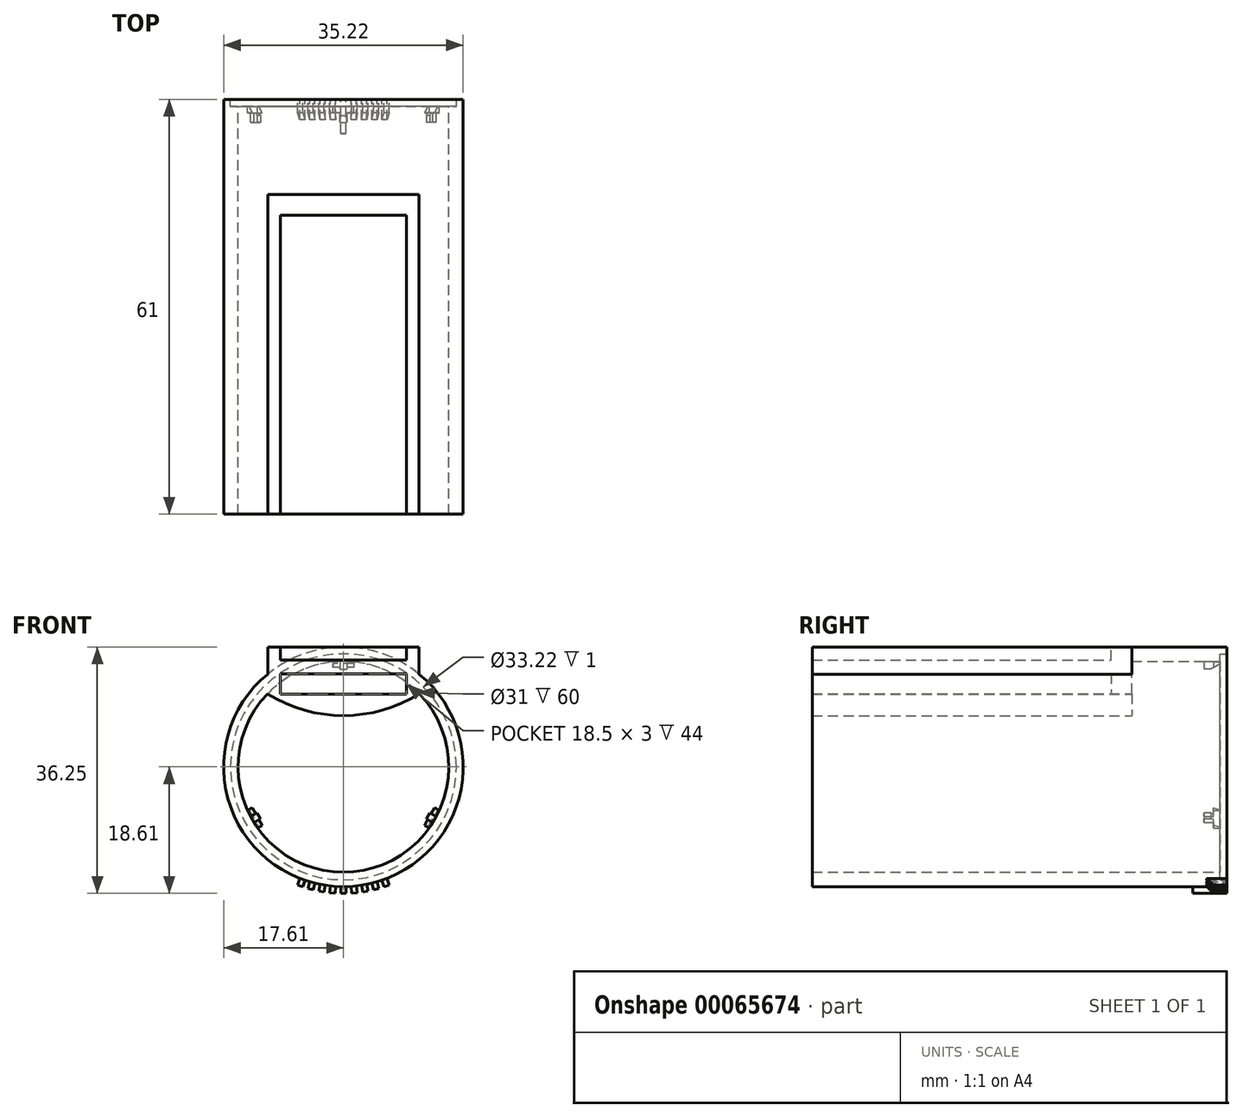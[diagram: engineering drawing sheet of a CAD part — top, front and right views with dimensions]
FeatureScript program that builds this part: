
annotation { "Feature Type Name" : "Feature", "Feature Type Description" : "" }
export const myFeature = defineFeature(function(context is Context, id is Id, definition is map)
    precondition{}
    {
        {
            var Q0;
            Q0=qCreatedBy(makeId("Front.planeOp"),FACE);
            var sketch = newSketch(context, id + "F0", { "sketchPlane" : qUnion([Q0])});
            skCircle(sketch, "E0", {"center": v(0, 0) * mm, "radius": 15.5 * mm});
            skCircle(sketch, "E1", {"center": v(0, 0) * mm, "radius": 17.6 * mm});
            skCircle(sketch, "E2", {"center": v(0, 0) * mm, "radius": 16.6 * mm});
            skPoint(sketch, "E3", {"position": v(0, 14.4) * mm});
            skLineSegment(sketch, "E4", {"start": v(0, 0) * mm, "end": v(0, 14.4) * mm, "construction": true});
            skSolve(sketch);
        }
        {
            var Q0;
            Q0=makeQuery(id+"F0.imprint","IMPRINT",FACE,{"disambiguationData":[TD([[makeQuery(id+"F0.imprint","IMPRINT",EDGE,{"derivedFrom":sQuery(id+"F0.wireOp",EDGE,"E1")}),1.0]])]});
            var sketch = newSketch(context, id + "F1", { "sketchPlane" : qUnion([Q0])});
            skCircle(sketch, "E5.0", {"center": v(0, 0) * mm, "radius": 17.6 * mm, "construction": true});
            skLineSegment(sketch, "E6", {"start": v(0, 0) * mm, "end": v(12.73, -34.98) * mm, "construction": true});
            skPoint(sketch, "E7", {"position": v(6.36, -17.49) * mm});
            skLineSegment(sketch, "E8", {"start": v(6.74, -17.35) * mm, "end": v(5.99, -17.62) * mm});
            skLineSegment(sketch, "E9", {"start": v(6.74, -17.35) * mm, "end": v(6.4, -16.4) * mm});
            skLineSegment(sketch, "E10", {"start": v(5.99, -17.62) * mm, "end": v(5.65, -16.68) * mm});
            skPoint(sketch, "E11.1.0", {"position": v(4.82, -17.98) * mm});
            skLineSegment(sketch, "E11.1.1", {"start": v(5.2, -17.87) * mm, "end": v(4.94, -16.9) * mm});
            skLineSegment(sketch, "E11.1.2", {"start": v(4.43, -18.08) * mm, "end": v(4.17, -17.1) * mm});
            skLineSegment(sketch, "E11.1.3", {"start": v(5.2, -17.87) * mm, "end": v(4.43, -18.08) * mm});
            skPoint(sketch, "E11.2.0", {"position": v(3.23, -18.33) * mm});
            skLineSegment(sketch, "E11.2.1", {"start": v(3.63, -18.26) * mm, "end": v(3.45, -17.27) * mm});
            skLineSegment(sketch, "E11.2.2", {"start": v(2.84, -18.4) * mm, "end": v(2.66, -17.4) * mm});
            skLineSegment(sketch, "E11.2.3", {"start": v(3.63, -18.26) * mm, "end": v(2.84, -18.4) * mm});
            skPoint(sketch, "E11.3.0", {"position": v(1.62, -18.54) * mm});
            skLineSegment(sketch, "E11.3.1", {"start": v(2.02, -18.5) * mm, "end": v(1.93, -17.5) * mm});
            skLineSegment(sketch, "E11.3.2", {"start": v(1.22, -18.57) * mm, "end": v(1.14, -17.57) * mm});
            skLineSegment(sketch, "E11.3.3", {"start": v(2.02, -18.5) * mm, "end": v(1.22, -18.57) * mm});
            skPoint(sketch, "E11.4.0", {"position": v(0, -18.61) * mm});
            skLineSegment(sketch, "E11.4.1", {"start": v(0.4, -18.61) * mm, "end": v(0.4, -17.6) * mm});
            skLineSegment(sketch, "E11.4.2", {"start": v(-0.4, -18.61) * mm, "end": v(-0.4, -17.6) * mm});
            skLineSegment(sketch, "E11.4.3", {"start": v(0.4, -18.61) * mm, "end": v(-0.4, -18.61) * mm});
            skPoint(sketch, "E11.5.0", {"position": v(-1.62, -18.54) * mm});
            skLineSegment(sketch, "E11.5.1", {"start": v(-1.22, -18.57) * mm, "end": v(-1.14, -17.57) * mm});
            skLineSegment(sketch, "E11.5.2", {"start": v(-2.02, -18.5) * mm, "end": v(-1.93, -17.5) * mm});
            skLineSegment(sketch, "E11.5.3", {"start": v(-1.22, -18.57) * mm, "end": v(-2.02, -18.5) * mm});
            skPoint(sketch, "E11.6.0", {"position": v(-3.23, -18.33) * mm});
            skLineSegment(sketch, "E11.6.1", {"start": v(-2.84, -18.4) * mm, "end": v(-2.66, -17.4) * mm});
            skLineSegment(sketch, "E11.6.2", {"start": v(-3.63, -18.26) * mm, "end": v(-3.45, -17.27) * mm});
            skLineSegment(sketch, "E11.6.3", {"start": v(-2.84, -18.4) * mm, "end": v(-3.63, -18.26) * mm});
            skPoint(sketch, "E11.7.0", {"position": v(-4.82, -17.98) * mm});
            skLineSegment(sketch, "E11.7.1", {"start": v(-4.43, -18.08) * mm, "end": v(-4.17, -17.1) * mm});
            skLineSegment(sketch, "E11.7.2", {"start": v(-5.2, -17.87) * mm, "end": v(-4.94, -16.9) * mm});
            skLineSegment(sketch, "E11.7.3", {"start": v(-4.43, -18.08) * mm, "end": v(-5.2, -17.87) * mm});
            skPoint(sketch, "E11.8.0", {"position": v(-6.36, -17.49) * mm});
            skLineSegment(sketch, "E11.8.1", {"start": v(-5.99, -17.62) * mm, "end": v(-5.65, -16.68) * mm});
            skLineSegment(sketch, "E11.8.2", {"start": v(-6.74, -17.35) * mm, "end": v(-6.4, -16.4) * mm});
            skLineSegment(sketch, "E11.8.3", {"start": v(-5.99, -17.62) * mm, "end": v(-6.74, -17.35) * mm});
            skLineSegment(sketch, "E11.anchor1", {"start": v(0, 0) * mm, "end": v(6.36, -17.49) * mm, "construction": true});
            skLineSegment(sketch, "E11.anchor2", {"start": v(0, 0) * mm, "end": v(-6.36, -17.49) * mm, "construction": true});
            skSolve(sketch);
        }
        {
            var Q0;
            Q0=qCreatedBy(makeId("Front.planeOp"),FACE);
            cPlane(context, id + "F2", {"entities" : qUnion([Q0]), "cplaneType" : CPlaneType.OFFSET, "offset" : 17 * mm, "width" : 150 * mm, "height" : 150 * mm});
        }
        {
            var Q0;
            Q0=qCreatedBy(id+"F2.planeOp",FACE);
            var sketch = newSketch(context, id + "F3", { "sketchPlane" : qUnion([Q0])});
            skLineSegment(sketch, "E12.rect.bottom", {"start": v(-9.25, 13.7) * mm, "end": v(9.25, 13.7) * mm});
            skLineSegment(sketch, "E12.rect.top", {"start": v(-9.25, 10.7) * mm, "end": v(9.25, 10.7) * mm});
            skLineSegment(sketch, "E12.rect.left", {"start": v(-9.25, 13.7) * mm, "end": v(-9.25, 10.7) * mm});
            skLineSegment(sketch, "E12.rect.right", {"start": v(9.25, 13.7) * mm, "end": v(9.25, 10.7) * mm});
            skPoint(sketch, "E12.rect.middle", {"position": v(0, 12.2) * mm});
            skLineSegment(sketch, "E13.rect.bottom", {"start": v(-6.75, 13.7) * mm, "end": v(6.75, 13.7) * mm});
            skLineSegment(sketch, "E13.rect.top", {"start": v(-6.75, 15.7) * mm, "end": v(6.75, 15.7) * mm});
            skLineSegment(sketch, "E13.rect.left", {"start": v(-6.75, 13.7) * mm, "end": v(-6.75, 15.7) * mm});
            skLineSegment(sketch, "E13.rect.right", {"start": v(6.75, 13.7) * mm, "end": v(6.75, 15.7) * mm});
            skPoint(sketch, "E13.rect.middle", {"position": v(0, 14.7) * mm});
            skLineSegment(sketch, "E14.rect.bottom", {"start": v(9.25, 15.7) * mm, "end": v(-9.25, 15.7) * mm});
            skLineSegment(sketch, "E14.rect.top", {"start": v(9.25, 18.83) * mm, "end": v(-9.25, 18.83) * mm});
            skLineSegment(sketch, "E14.rect.left", {"start": v(9.25, 15.7) * mm, "end": v(9.25, 18.83) * mm});
            skLineSegment(sketch, "E14.rect.right", {"start": v(-9.25, 15.7) * mm, "end": v(-9.25, 18.83) * mm});
            skPoint(sketch, "E14.rect.middle", {"position": v(0, 17.26) * mm});
            skPoint(sketch, "E14.rect.middle.positionSnap0", {"position": v(0, 15.7) * mm});
            skPoint(sketch, "E14.rect.cornerSnap0", {"position": v(0, 15.7) * mm});
            skPoint(sketch, "E14.rect.centerSnap0", {"position": v(0, 15.7) * mm});
            skSolve(sketch);
        }
        {
            var Q0;
            Q0=qCreatedBy(id+"F2.planeOp",FACE);
            var sketch = newSketch(context, id + "F4", { "sketchPlane" : qUnion([Q0])});
            skLineSegment(sketch, "E15.rect.bottom", {"start": v(-11.14, 17.64) * mm, "end": v(11.14, 17.64) * mm});
            skLineSegment(sketch, "E15.rect.top", {"start": v(-11.14, 10.71) * mm, "end": v(11.14, 10.71) * mm});
            skLineSegment(sketch, "E15.rect.left", {"start": v(-11.14, 17.64) * mm, "end": v(-11.14, 10.71) * mm});
            skLineSegment(sketch, "E15.rect.right", {"start": v(11.14, 17.64) * mm, "end": v(11.14, 10.71) * mm});
            skPoint(sketch, "E15.rect.middle", {"position": v(0, 14.18) * mm});
            skArc(sketch, "E16", {"start": v(-11.14, 10.71) * mm, "mid": v(0, 7.54) * mm, "end": v(11.14, 10.71) * mm});
            skPoint(sketch, "E16.third.point", {"position": v(-1.83, 7.62) * mm});
            skSolve(sketch);
        }
        {
            var Q0;
            Q0=makeQuery(id+"F0.imprint","IMPRINT",FACE,{"disambiguationData":[TD([[makeQuery(id+"F0.imprint","IMPRINT",EDGE,{"derivedFrom":sQuery(id+"F0.wireOp",EDGE,"E1")}),1.0]])]});
            extrude(context, id + "F5", {"entities" : qUnion([Q0]), "depth" : 61 * mm});
        }
        {
            var Q0;
            Q0=makeQuery(id+"F0.imprint","IMPRINT",FACE,{"disambiguationData":[TD([[makeQuery(id+"F0.imprint","IMPRINT",EDGE,{"derivedFrom":sQuery(id+"F0.wireOp",EDGE,"E0")}),-1.0]])]});
            var Q1;
            Q1=makeQuery(id+"F5.opExtrude","CAP_FACE",FACE,{"disambiguationData":[OSD([sQuery(id+"F0.wireOp",EDGE,"E1"),sQuery(id+"F0.wireOp",EDGE,"E2")])],"isStart":false});
            extrude(context, id + "F6", {"entities" : qUnion([Q0]), "operationType" : NewBodyOperationType.ADD, "endBound" : BoundingType.UP_TO_SURFACE, "endBoundEntityFace" : qUnion([Q1]), "depth" : 25 * mm, "hasSecondDirection" : true, "secondDirectionOppositeDirection" : false, "secondDirectionDepth" : 1 * mm});
        }
        {
            var Q0;
            Q0=sQuery(id+"F0.wireOp",VERTEX,"E3");
            var Q1;
            Q1=sQuery(id+"F0.wireOp",EDGE,"E4");
            cPlane(context, id + "F7", {"entities" : qUnion([Q0, Q1]), "cplaneType" : CPlaneType.LINE_POINT, "offset" : 150 * mm, "width" : 150 * mm, "height" : 150 * mm});
        }
        {
            var Q0;
            Q0=qCreatedBy(id+"F7.planeOp",FACE);
            var sketch = newSketch(context, id + "F8", { "sketchPlane" : qUnion([Q0])});
            skPoint(sketch, "E17.orphan", {"position": v(-15.5, -1) * mm});
            skPoint(sketch, "E18.orphan", {"position": v(15.5, -1) * mm});
            skLineSegment(sketch, "E19", {"start": v(-0.5, -3.4) * mm, "end": v(0, -3.4) * mm});
            skLineSegment(sketch, "E20", {"start": v(-0.5, -2) * mm, "end": v(-0.5, -3.4) * mm});
            skLineSegment(sketch, "E21", {"start": v(-0.5, -2) * mm, "end": v(-1.5, -2) * mm});
            skLineSegment(sketch, "E22", {"start": v(-1.5, -1) * mm, "end": v(-1.5, -2) * mm});
            skLineSegment(sketch, "E23", {"start": v(-1.5, -1) * mm, "end": v(0, -1) * mm});
            skLineSegment(sketch, "E24", {"start": v(0, -3.4) * mm, "end": v(0, 0) * mm, "construction": true});
            skLineSegment(sketch, "E25.MirrorCS", {"start": v(1.5, -1) * mm, "end": v(0, -1) * mm});
            skLineSegment(sketch, "E26.MirrorCS", {"start": v(1.5, -1) * mm, "end": v(1.5, -2) * mm});
            skLineSegment(sketch, "E27.MirrorCS", {"start": v(0.5, -2) * mm, "end": v(1.5, -2) * mm});
            skLineSegment(sketch, "E28.MirrorCS", {"start": v(0.5, -2) * mm, "end": v(0.5, -3.4) * mm});
            skLineSegment(sketch, "E29.MirrorCS", {"start": v(0.5, -3.4) * mm, "end": v(0, -3.4) * mm});
            skLineSegment(sketch, "E30.0", {"start": v(15.5, -1) * mm, "end": v(-15.5, -1) * mm, "construction": true});
            skSolve(sketch);
        }
        {
            var Q0;
            Q0=makeQuery(id+"F8.imprint","IMPRINT",FACE,{"disambiguationData":[TD([[makeQuery(id+"F8.imprint","IMPRINT",EDGE,{"derivedFrom":sQuery(id+"F8.wireOp",EDGE,"E19")}),1.0]])]});
            var Q1;
            Q1=makeQuery(id+"F6.opExtrude","SWEPT_FACE",FACE,{"disambiguationData":[OSD([sQuery(id+"F0.wireOp",EDGE,"E0")])]});
            extrude(context, id + "F9", {"entities" : qUnion([Q0]), "endBound" : BoundingType.UP_TO_SURFACE, "endBoundEntityFace" : qUnion([Q1]), "depth" : 25 * mm});
        }
        {
            var Q0;
            Q0=makeQuery(id+"F9.opExtrude","CAP_EDGE",EDGE,{"disambiguationData":[OSD([sQuery(id+"F8.wireOp",EDGE,"E23"),sQuery(id+"F8.wireOp",EDGE,"E25.MirrorCS")])],"isStart":true});
            chamfer(context, id + "F10", {"entities" : qUnion([Q0]), "chamferType" : ChamferType.OFFSET_ANGLE, "width" : 0.8 * mm, "oppositeDirection" : false, "angle" : 60 * degree, "tangentPropagation" : true});
        }
        {
            var Q0;
            Q0=qCreatedBy(makeId("Right.planeOp"),FACE);
            var sketch = newSketch(context, id + "F11", { "sketchPlane" : qUnion([Q0])});
            skLineSegment(sketch, "E31", {"start": v(0, 0) * mm, "end": v(-69.37, 0) * mm, "construction": true});
            skSolve(sketch);
        }
        {
            var Q0;
            Q0=makeQuery(id+"F9.opExtrude","SWEPT_BODY",BODY,{"disambiguationData":[OSD([sQuery(id+"F8.wireOp",EDGE,"E19"),sQuery(id+"F8.wireOp",EDGE,"E20"),sQuery(id+"F8.wireOp",EDGE,"E21"),sQuery(id+"F8.wireOp",EDGE,"E22"),sQuery(id+"F8.wireOp",EDGE,"E23"),sQuery(id+"F8.wireOp",EDGE,"E25.MirrorCS"),sQuery(id+"F8.wireOp",EDGE,"E26.MirrorCS"),sQuery(id+"F8.wireOp",EDGE,"E27.MirrorCS"),sQuery(id+"F8.wireOp",EDGE,"E28.MirrorCS"),sQuery(id+"F8.wireOp",EDGE,"E29.MirrorCS")])]});
            var Q1;
            Q1=sQuery(id+"F11.wireOp",EDGE,"E31");
            circularPattern(context, id + "F12", {"entities" : qUnion([Q0]), "axis" : qUnion([Q1]), "angle" : 360 * degree, "instanceCount" : 3, "equalSpace" : true});
        }
        {
            var Q0;
            Q0=makeQuery(id+"F4.imprint","IMPRINT",FACE,{"disambiguationData":[TD([[makeQuery(id+"F4.imprint","IMPRINT",EDGE,{"derivedFrom":sQuery(id+"F4.wireOp",EDGE,"E15.rect.bottom")}),-1.0]])]});
            var Q1;
            Q1=makeQuery(id+"F4.imprint","IMPRINT",FACE,{"disambiguationData":[TD([[makeQuery(id+"F4.imprint","IMPRINT",EDGE,{"derivedFrom":sQuery(id+"F4.wireOp",EDGE,"E15.rect.top")}),-1.0]])]});
            var Q2;
            {var subQ0=sQuery(id+"F0.wireOp",EDGE,"E2");Q2=makeQuery(id+"F6.boolean.opBoolean","MERGE",FACE,{"derivedFrom":[makeQuery(id+"F5.opExtrude","CAP_FACE",FACE,{"disambiguationData":[OSD([sQuery(id+"F0.wireOp",EDGE,"E1"),subQ0])],"isStart":false}),makeQuery(id+"F6.opExtrude","CAP_FACE",FACE,{"disambiguationData":[OSD([sQuery(id+"F0.wireOp",EDGE,"E0"),subQ0])],"isStart":false})]});}
            var Q3;
            Q3=makeQuery(id+"F5.opExtrude","SWEPT_BODY",BODY,{"disambiguationData":[OSD([sQuery(id+"F0.wireOp",EDGE,"E1"),sQuery(id+"F0.wireOp",EDGE,"E2")])]});
            extrude(context, id + "F13", {"entities" : qUnion([Q0, Q1]), "operationType" : NewBodyOperationType.ADD, "endBound" : BoundingType.UP_TO_SURFACE, "endBoundEntityFace" : qUnion([Q2]), "endBoundEntityBody" : qUnion([Q3]), "depth" : 25 * mm, "hasSecondDirection" : true, "secondDirectionOppositeDirection" : true, "secondDirectionDepth" : 3 * mm});
        }
        {
            var Q0;
            Q0=makeQuery(id+"F3.imprint","IMPRINT",FACE,{"disambiguationData":[TD([[makeQuery(id+"F3.imprint","IMPRINT",EDGE,{"derivedFrom":sQuery(id+"F3.wireOp",EDGE,"E12.rect.top")}),1.0]])]});
            var Q1;
            Q1=makeQuery(id+"F3.imprint","IMPRINT",FACE,{"disambiguationData":[TD([[makeQuery(id+"F3.imprint","IMPRINT",EDGE,{"derivedFrom":sQuery(id+"F3.wireOp",EDGE,"E13.rect.bottom")}),1.0]])]});
            var Q2;
            Q2=makeQuery(id+"F3.imprint","IMPRINT",FACE,{"disambiguationData":[TD([[makeQuery(id+"F3.imprint","IMPRINT",EDGE,{"derivedFrom":sQuery(id+"F3.wireOp",EDGE,"E14.rect.top")}),1.0]])]});
            var Q3;
            {var subQ0=sQuery(id+"F0.wireOp",EDGE,"E2");Q3=makeQuery(id+"F13.boolean.opBoolean","MERGE",FACE,{"derivedFrom":[makeQuery(id+"F6.boolean.opBoolean","MERGE",FACE,{"derivedFrom":[makeQuery(id+"F5.opExtrude","CAP_FACE",FACE,{"disambiguationData":[OSD([sQuery(id+"F0.wireOp",EDGE,"E1"),subQ0])],"isStart":false}),makeQuery(id+"F6.opExtrude","CAP_FACE",FACE,{"disambiguationData":[OSD([sQuery(id+"F0.wireOp",EDGE,"E0"),subQ0])],"isStart":false})]}),makeQuery(id+"F13.opExtrude","CAP_FACE",FACE,{"disambiguationData":[OSD([sQuery(id+"F4.wireOp",EDGE,"E15.rect.bottom"),sQuery(id+"F4.wireOp",EDGE,"E15.rect.top"),sQuery(id+"F4.wireOp",EDGE,"E15.rect.left"),sQuery(id+"F4.wireOp",EDGE,"E15.rect.right")])],"isStart":false})]});}
            extrude(context, id + "F14", {"entities" : qUnion([Q0, Q1, Q2]), "operationType" : NewBodyOperationType.REMOVE, "endBound" : BoundingType.UP_TO_SURFACE, "endBoundEntityFace" : qUnion([Q3]), "depth" : 25 * mm});
        }
        {
            var Q0;
            Q0=qCreatedBy(makeId("Front.planeOp"),FACE);
            var sketch = newSketch(context, id + "F15", { "sketchPlane" : qUnion([Q0])});
            skLineSegment(sketch, "E32.bottom", {"start": v(-25.03, -23.24) * mm, "end": v(25.28, -23.24) * mm});
            skLineSegment(sketch, "E32.top", {"start": v(-25.03, 20.09) * mm, "end": v(25.28, 20.09) * mm});
            skLineSegment(sketch, "E32.left", {"start": v(-25.03, -23.24) * mm, "end": v(-25.03, 20.09) * mm});
            skLineSegment(sketch, "E32.right", {"start": v(25.28, -23.24) * mm, "end": v(25.28, 20.09) * mm});
            skSolve(sketch);
        }
        {
            var Q0;
            Q0=makeQuery(id+"F1.imprint","IMPRINT",FACE,{"disambiguationData":[TD([[makeQuery(id+"F1.imprint","IMPRINT",EDGE,{"derivedFrom":sQuery(id+"F1.wireOp",EDGE,"E8")}),-1.0]])]});
            var Q1;
            {var subQ0=sQuery(id+"F1.wireOp",EDGE,"E11.1.1");Q1=makeQuery(id+"F1.imprint","IMPRINT",FACE,{"disambiguationData":[TD([[makeQuery(id+"F1.imprint","IMPRINT",EDGE,{"derivedFrom":subQ0}),1.0]])]});}
            var Q2;
            {var subQ0=sQuery(id+"F1.wireOp",EDGE,"E11.2.1");Q2=makeQuery(id+"F1.imprint","IMPRINT",FACE,{"disambiguationData":[TD([[makeQuery(id+"F1.imprint","IMPRINT",EDGE,{"derivedFrom":subQ0}),1.0]])]});}
            var Q3;
            {var subQ0=sQuery(id+"F1.wireOp",EDGE,"E11.3.1");Q3=makeQuery(id+"F1.imprint","IMPRINT",FACE,{"disambiguationData":[TD([[makeQuery(id+"F1.imprint","IMPRINT",EDGE,{"derivedFrom":subQ0}),1.0]])]});}
            var Q4;
            {var subQ0=sQuery(id+"F1.wireOp",EDGE,"E11.8.1");Q4=makeQuery(id+"F1.imprint","IMPRINT",FACE,{"disambiguationData":[TD([[makeQuery(id+"F1.imprint","IMPRINT",EDGE,{"derivedFrom":subQ0}),1.0]])]});}
            var Q5;
            {var subQ0=sQuery(id+"F1.wireOp",EDGE,"E11.7.1");Q5=makeQuery(id+"F1.imprint","IMPRINT",FACE,{"disambiguationData":[TD([[makeQuery(id+"F1.imprint","IMPRINT",EDGE,{"derivedFrom":subQ0}),1.0]])]});}
            var Q6;
            {var subQ0=sQuery(id+"F1.wireOp",EDGE,"E11.6.1");Q6=makeQuery(id+"F1.imprint","IMPRINT",FACE,{"disambiguationData":[TD([[makeQuery(id+"F1.imprint","IMPRINT",EDGE,{"derivedFrom":subQ0}),1.0]])]});}
            var Q7;
            {var subQ0=sQuery(id+"F1.wireOp",EDGE,"E11.5.1");Q7=makeQuery(id+"F1.imprint","IMPRINT",FACE,{"disambiguationData":[TD([[makeQuery(id+"F1.imprint","IMPRINT",EDGE,{"derivedFrom":subQ0}),1.0]])]});}
            var Q8;
            {var subQ0=sQuery(id+"F1.wireOp",EDGE,"E11.4.1");Q8=makeQuery(id+"F1.imprint","IMPRINT",FACE,{"disambiguationData":[TD([[makeQuery(id+"F1.imprint","IMPRINT",EDGE,{"derivedFrom":subQ0}),1.0]])]});}
            extrude(context, id + "F16", {"entities" : qUnion([Q0, Q1, Q2, Q3, Q4, Q5, Q6, Q7, Q8]), "operationType" : NewBodyOperationType.ADD, "depth" : 5 * mm});
        }
        {
            var Q0;
            Q0=makeQuery(id+"F16.opExtrude","CAP_EDGE",EDGE,{"disambiguationData":[OSD([sQuery(id+"F1.wireOp",EDGE,"E11.8.3")])],"isStart":false});
            var Q1;
            Q1=makeQuery(id+"F16.opExtrude","CAP_EDGE",EDGE,{"disambiguationData":[OSD([sQuery(id+"F1.wireOp",EDGE,"E11.7.3")])],"isStart":false});
            var Q2;
            Q2=makeQuery(id+"F16.opExtrude","CAP_EDGE",EDGE,{"disambiguationData":[OSD([sQuery(id+"F1.wireOp",EDGE,"E11.6.3")])],"isStart":false});
            var Q3;
            Q3=makeQuery(id+"F16.opExtrude","CAP_EDGE",EDGE,{"disambiguationData":[OSD([sQuery(id+"F1.wireOp",EDGE,"E11.5.3")])],"isStart":false});
            var Q4;
            Q4=makeQuery(id+"F16.opExtrude","CAP_EDGE",EDGE,{"disambiguationData":[OSD([sQuery(id+"F1.wireOp",EDGE,"E11.3.3")])],"isStart":false});
            var Q5;
            Q5=makeQuery(id+"F16.opExtrude","CAP_EDGE",EDGE,{"disambiguationData":[OSD([sQuery(id+"F1.wireOp",EDGE,"E11.2.3")])],"isStart":false});
            var Q6;
            Q6=makeQuery(id+"F16.opExtrude","CAP_EDGE",EDGE,{"disambiguationData":[OSD([sQuery(id+"F1.wireOp",EDGE,"E11.1.3")])],"isStart":false});
            var Q7;
            Q7=makeQuery(id+"F16.opExtrude","CAP_EDGE",EDGE,{"disambiguationData":[OSD([sQuery(id+"F1.wireOp",EDGE,"E8")])],"isStart":false});
            chamfer(context, id + "F17", {"entities" : qUnion([Q0, Q1, Q2, Q3, Q4, Q5, Q6, Q7]), "width" : 3 * mm, "tangentPropagation" : true});
        }
    });
